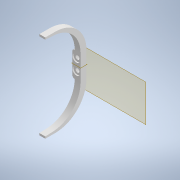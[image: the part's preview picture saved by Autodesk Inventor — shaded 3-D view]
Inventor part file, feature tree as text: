
AUTODESK INVENTOR PART (.ipt)
format: ipt  version: 2020 (Build 240168000, 168)  size: 157,696 bytes
history: native  units: mm
features: sketch x3, other x3, plane x2, extrude x2, hole x1, mirror x1, reference x1
ambient origin geometry x8: Origin, YZ Plane, XZ Plane, XY Plane, X Axis, Y Axis, Z Axis, Center Point
bodies: Solid1 (feature_tree)
feature tree (13):
  plane  "Work Plane1"
  extrude  "Extrusion1"  Depth=1.0mm
  plane  "Work Plane2"
  extrude  "Extrusion2"  Depth=35.0mm
  hole  "Hole1"  [1 undecoded]
  mirror  "Mirror1"
  sketch  "Sketch1"  dims[d0=5.0mm d1=0.0mm]
  reference  "Reference1"
  sketch  "Sketch2"  dims[d2=3.2mm d3=6.0mm d4=6.5mm d5=1.0mm d6=90.0deg d7=8.0mm d8=20.594885mm d9=3.0mm]
  sketch  "Sketch3"  dims[d10=5.0mm d11=0.0mm d12=35.0mm]
  parser-record x1  (decoder bookkeeping rows leaked as tree rows — omitted from the tree; the rows remain in map.json)
  other  "motorized.iam"
  other  "bracket:1"
note: 1 required parameter value undecoded (feature->parameter linkage not recoverable at this tier; creation-order binding heuristic only, values carry confidence <= 0.55)
note: 1 file-system path scrubbed to <path> (originals preserved in map.json)
